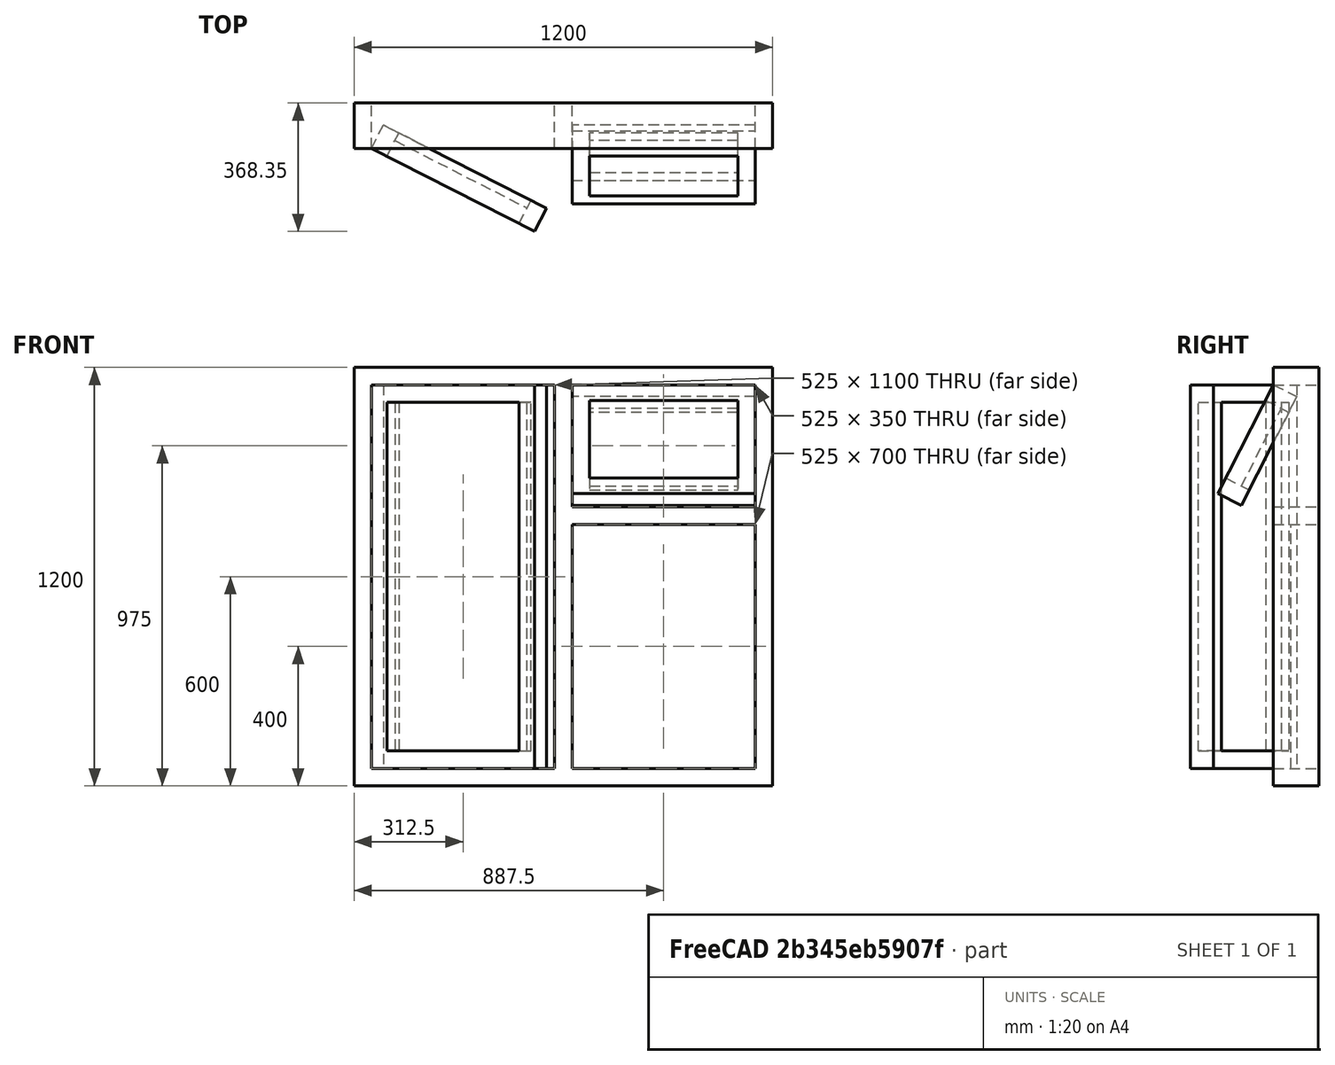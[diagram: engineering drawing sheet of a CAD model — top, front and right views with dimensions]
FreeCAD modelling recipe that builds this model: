
FCSTD DOCUMENT  (FreeCAD 0.19R23578 (Git))
Label: ThreePartLeft
License: Creative Commons Attribution-ShareAlike
LicenseURL: http://creativecommons.org/licenses/by-sa/4.0/
objects: Sketcher::SketchObject×1, Part::FeaturePython×1
note: 2 computed .brp shape members not serialized (recipe doc carries the construction recipe); baked Part::Feature solids carry a one-line shape summary decoded from their .brp

FEATURE [Sketcher::SketchObject] Sketch
  Placement = pos=(0,0,0) rot=(1,0,0;1.5708rad)
  expr: .Constraints.WidthSide = (.Constraints.Width - 3 * .Constraints.Frame) / 2
  expr: .Constraints.FrameOpen = .Constraints.Frame
  sketch-geometry (41):
    g0: LineSegment StartX=0 StartY=0 StartZ=0 EndX=1200 EndY=0 EndZ=0
    g1: LineSegment StartX=1200 StartY=0 StartZ=0 EndX=1200 EndY=1200 EndZ=0
    g2: LineSegment StartX=1200 StartY=1200 StartZ=0 EndX=0 EndY=1200 EndZ=0
    g3: LineSegment StartX=0 StartY=1200 StartZ=0 EndX=0 EndY=0 EndZ=0
    g4: LineSegment StartX=625 StartY=50 StartZ=0 EndX=1150 EndY=50 EndZ=0
    g5: LineSegment StartX=1150 StartY=50 StartZ=0 EndX=1150 EndY=750 EndZ=0
    g6: LineSegment StartX=1150 StartY=750 StartZ=0 EndX=625 EndY=750 EndZ=0
    g7: LineSegment StartX=625 StartY=750 StartZ=0 EndX=625 EndY=50 EndZ=0
    g8: LineSegment StartX=625 StartY=800 StartZ=0 EndX=1150 EndY=800 EndZ=0
    g9: LineSegment StartX=1150 StartY=800 StartZ=0 EndX=1150 EndY=1150 EndZ=0
    g10: LineSegment StartX=1150 StartY=1150 StartZ=0 EndX=625 EndY=1150 EndZ=0
    g11: LineSegment StartX=625 StartY=1150 StartZ=0 EndX=625 EndY=800 EndZ=0
    g12: LineSegment StartX=675 StartY=850 StartZ=0 EndX=1100 EndY=850 EndZ=0
    g13: LineSegment StartX=1100 StartY=850 StartZ=0 EndX=1100 EndY=1100 EndZ=0
    g14: LineSegment StartX=1100 StartY=1100 StartZ=0 EndX=675 EndY=1100 EndZ=0
    g15: LineSegment StartX=675 StartY=1100 StartZ=0 EndX=675 EndY=850 EndZ=0
    g16: LineSegment StartX=50 StartY=50 StartZ=0 EndX=575 EndY=50 EndZ=0
    g17: LineSegment StartX=575 StartY=50 StartZ=0 EndX=575 EndY=1150 EndZ=0
    g18: LineSegment StartX=575 StartY=1150 StartZ=0 EndX=50 EndY=1150 EndZ=0
    g19: LineSegment StartX=50 StartY=1150 StartZ=0 EndX=50 EndY=50 EndZ=0
    g20: LineSegment StartX=100 StartY=100 StartZ=0 EndX=525 EndY=100 EndZ=0
    g21: LineSegment StartX=525 StartY=100 StartZ=0 EndX=525 EndY=1100 EndZ=0
    g22: LineSegment StartX=525 StartY=1100 StartZ=0 EndX=100 EndY=1100 EndZ=0
    g23: LineSegment StartX=100 StartY=1100 StartZ=0 EndX=100 EndY=100 EndZ=0
    g24: LineSegment StartX=50 StartY=50 StartZ=0 EndX=50 EndY=0 EndZ=0
    g25: LineSegment StartX=100 StartY=1100 StartZ=0 EndX=50 EndY=1100 EndZ=0
    g26: LineSegment StartX=100 StartY=1100 StartZ=0 EndX=100 EndY=1150 EndZ=0
    g27: LineSegment StartX=525 StartY=100 StartZ=0 EndX=575 EndY=100 EndZ=0
    g28: LineSegment StartX=1150 StartY=1150 StartZ=0 EndX=1150 EndY=1200 EndZ=0
    g29: LineSegment StartX=1100 StartY=850 StartZ=0 EndX=1100 EndY=800 EndZ=0
    g30: LineSegment StartX=1100 StartY=850 StartZ=0 EndX=1150 EndY=850 EndZ=0
    g31: LineSegment StartX=675 StartY=1100 StartZ=0 EndX=625 EndY=1100 EndZ=0
    g32: LineSegment StartX=50 StartY=50 StartZ=0 EndX=0 EndY=0 EndZ=0
    g33: LineSegment StartX=1150 StartY=750 StartZ=0 EndX=1200 EndY=750 EndZ=0
    g34: LineSegment StartX=1200 StartY=750 StartZ=0 EndX=1150 EndY=800 EndZ=0
    g35: LineSegment StartX=1150 StartY=50 StartZ=0 EndX=1150 EndY=0 EndZ=0
    g36: LineSegment StartX=1200 StartY=0 StartZ=0 EndX=1150 EndY=50 EndZ=0
    g37: LineSegment StartX=1150 StartY=1150 StartZ=0 EndX=1200 EndY=1200 EndZ=0
    g38: LineSegment StartX=525 StartY=100 StartZ=0 EndX=575 EndY=50 EndZ=0
    g39: LineSegment StartX=575 StartY=50 StartZ=0 EndX=625 EndY=0 EndZ=0
    g40: LineSegment StartX=625 StartY=50 StartZ=0 EndX=625 EndY=0 EndZ=0
  constraints (116):
    c: Coincident(g0,g1)
    c: Coincident(g1,g2)
    c: Coincident(g2,g3)
    c: Coincident(g3,g0)
    c: Horizontal(g2)
    c: Vertical(g1)
    c: Vertical(g3)
    c: Coincident(g0,g-1)
    c: Coincident(g4,g5)
    c: Coincident(g5,g6)
    c: Coincident(g6,g7)
    c: Coincident(g7,g4)
    c: Horizontal(g4)
    c: Horizontal(g6)
    c: Vertical(g5)
    c: Vertical(g7)
    c: Coincident(g8,g9)
    c: Coincident(g9,g10)
    c: Coincident(g10,g11)
    c: Coincident(g11,g8)
    c: Horizontal(g8)
    c: Horizontal(g10)
    c: Vertical(g9)
    c: Vertical(g11)
    c: Coincident(g12,g13)
    c: Coincident(g13,g14)
    c: Coincident(g14,g15)
    c: Coincident(g15,g12)
    c: Horizontal(g12)
    c: Horizontal(g14)
    c: Vertical(g13)
    c: Vertical(g15)
    c: Coincident(g16,g17)
    c: Coincident(g17,g18)
    c: Coincident(g18,g19)
    c: Coincident(g19,g16)
    c: Horizontal(g16)
    c: Horizontal(g18)
    c: Vertical(g17)
    c: Vertical(g19)
    c: Coincident(g20,g21)
    c: Coincident(g21,g22)
    c: Coincident(g22,g23)
    c: Coincident(g23,g20)
    c: Horizontal(g20)
    c: Horizontal(g22)
    c: Vertical(g21)
    c: Vertical(g23)
    c: Horizontal(g17,g10)
    c: Horizontal(g21,g14)
    c: Vertical(g8,g6)
    c: Vertical(g5,g8)
    c: Coincident(g24,g16)
    c: PointOnObject(g24,g0)
    c: Vertical(g24)
    c: Coincident(g25,g22)
    c: PointOnObject(g25,g19)
    c: Horizontal(g25)
    c: Coincident(g26,g22)
    c: PointOnObject(g26,g18)
    c: Vertical(g26)
    c: Coincident(g27,g20)
    c: PointOnObject(g27,g17)
    c: Horizontal(g27)
    c: Coincident(g28,g9)
    c: PointOnObject(g28,g2)
    c: Vertical(g28)
    c: Coincident(g29,g12)
    c: PointOnObject(g29,g8)
    c: Vertical(g29)
    c: Coincident(g30,g12)
    c: PointOnObject(g30,g9)
    c: Horizontal(g30)
    c: Coincident(g31,g14)
    c: PointOnObject(g31,g11)
    c: Horizontal(g31)
    c: DistanceY(g24,g24) = 50  'Frame'
    c: DistanceY(g26,g26) = 50  'FrameOpen'
    c: Equal(g25,g26)
    c: Equal(g26,g31)
    c: Equal(g27,g29)
    c: Equal(g29,g30)
    c: DistanceY(g3,g3) = 1200  'Height'
    c: DistanceX(g0,g0) = 1200  'Width'
    c: DistanceY(g9,g9) = 350  'HeightTop'
    c: DistanceX(g18,g18) = 525  'WidthSide'
    c: Coincident(g32,g16)
    c: Coincident(g32,g0)
    c: Angle(g32,g24) = 0.785398
    c: Coincident(g33,g5)
    c: PointOnObject(g33,g1)
    c: Horizontal(g33)
    c: Coincident(g34,g33)
    c: Coincident(g34,g8)
    c: Angle(g34,g33) = 0.785398
    c: Coincident(g35,g4)
    c: PointOnObject(g35,g0)
    c: Vertical(g35)
    c: Coincident(g36,g0)
    c: Coincident(g36,g4)
    c: Coincident(g37,g9)
    c: Coincident(g37,g1)
    c: Angle(g37,g28) = 0.785398
    c: Coincident(g38,g20)
    c: Coincident(g38,g16)
    c: Angle(g38,g27) = 0.785398
    c: Equal(g27,g26)
    c: Coincident(g39,g16)
    c: Coincident(g40,g4)
    c: Coincident(g40,g39)
    c: Vertical(g40)
    c: Angle(g40,g39) = 0.785398
    c: PointOnObject(g39,g0)
    c: Angle(g35,g36) = 0.785398
    c: Horizontal(g4,g16)
    c: Parallel(g0,g4)
FEATURE [Part::FeaturePython] Window  # Arch/BIM 170 (typed FeaturePython)
  Area = 0
  Base = -> Sketch
  Frame = 0
  Height = 0
  HoleDepth = 0
  HoleWire = 1
  HorizontalArea = 0
  IfcData = attributes={"GlobalId": {"name": "GlobalId", "type": "IfcGloballyUniqueId", "is_enum": false, "enum_values": []}, "Description": {"... (+1225 chars omitted),+1 more (map truncated)
  IfcType = 170
  LouvreSpacing = 0
  LouvreWidth = 0
  MoveBase = true
  MoveWithHost = true
  Normal = (0,1,0)
  Opening = 30
  OverallHeight = 0
  OverallWidth = 0
  PartitioningType = 0
  PerimeterLength = 0
  PredefinedType = 0
  Preset = 0
  SymbolElevation = false
  SymbolPlan = false
  VerticalArea = 0
  Width = 0
  WindowParts = OuterFrame | Frame | Wire0,Wire1,Wire2,Wire4 | 130.0 | 0.0 | FixedGlass | Glass panel | Wire1 | 50 | 0.0 | TopFrame | Frame | Wire3,Wire2,Edge11,Mode1 | 75 | 0.0 | TopGlass | Glass panel | Wire3 | 50 | 0.0 | LeftFrame | Frame | Wire5,Wire4,Edge20,Mode2 | 75 | 0.0 | LeftGlass | Glass panel | Wire5 | 50 | 0.0
  expr: OverallWidth = .Width.Value
  expr: OverallHeight = .Height.Value
